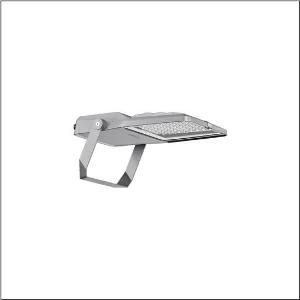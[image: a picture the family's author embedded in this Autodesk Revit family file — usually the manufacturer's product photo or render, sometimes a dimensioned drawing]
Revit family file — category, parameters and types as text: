
# Revit family: floodlight_fl_21_iq_mini___pl64_5xa7771b2e1a_713d
name_source: partatom
category: Lighting Fixtures
units: mm (PartAtom-declared; Revit-internal decimal feet)

## family parameters
Cut with Voids When Loaded = No
Host = Face
Light Source = No
Part Type = Normal
Room Calculation Point = No
Round Connector Dimension = Use Diameter
Shared = No

## types (1)
- --- (1 x LED, 6020 lm, 45.5 W, 3000K)
    Apparent Load = 46 VA
    CIE Flux Codes = 28 80 98 100 100
    Color Rendering = 70
    Color Temperature = 3000K
    Default Elevation = 1800 mm
    Description = Floodlight FL 21 iQ mini, floodlight, primary light control with lens, of PMMA, primary optical cover: protective disc, of toughened safety glass, transparent, light distribution: PL64, light emission: direct distribution, installation type: surface-mounted, LED, High Power LED, rated luminous flux: 6.020lm, luminous efficacy: 132lm/W, light colour: 730, colour temperature: 3000K, control: Auto-Match, Temp-Guard, Lumen-Switch, Night-Set, Smart-Wire, Light-Fading, Desk-Remote (wireless, voltage-free reading and setting of iQ features in the workshop via application-optimized NFC function/RFID function), optimised constant luminous flux control (CLO 2.0), with terminal, 6-pole, mains connection: 220..240V, AC, 50/60Hz, start of lifetime: 46W, end of service life: 48W, reduction: 22W, luminaire housing, of diecast aluminium, powder-coated, Siteco® metallic grey (DB 702S), corrosivity category C5 mid according to DIN EN ISO 12944, sealing non-destructively replaceable, mounting bracket, of steel, galvanised, powder-coated, Siteco® metallic grey (DB 702S), protection rating (complete): IP66, insulation class (complete): insulation class II (safety insulation), certification: CE, ENEC, VDE, protection symbol: D, impact resistance: IK08, permissible operating ambient temperature: -40..+40°C, permissible operating ambient temperature for outdoor applications: -40..+50°C, standard: DIN EN 12944, LABS conformity tested according to VDMA 24364:2018-05, packaging unit: 1 piece

Light Distribution: PL64
    Height = 70 mm
    Lamp = 1 x LED
    Lamp Light Flux = 6020 lm
    Lamp Power = 45.5 W
    Lamp count = 1
    Length = 485 mm
    Luminous efficacy = 132 lm/W
    Manufacturer = Siteco
    ModVariant = No
    Model = 5XA7771B2E1A
    Mounting Place = Wall
    Mounting Type = Surface mounted
    Number of Poles = 1
    OnlyDefault = Yes
    Power Factor = 1
    Product Name = Floodlight FL 21 iQ mini | PL64
    Product group = floodlight | wall mounted
    ProductGroupID = 2001
    Protection Class = Protection class II
    Protection Degree = IP 66
    RLX_Detail_Level = 1
    RLX_Emergency_Light_Flux = 0 lm
    RLX_Emergency_Type = 0
    RLX_Emergency_Type_DB = No
    RlxData = <blob elided: 96197 chars, md5=8cffde66>
    Socket = socket
    Standby Power = 0 W
    System Light Flux = 6020 lm
    System Power = 46 W
    Type Comments = factory setting: luminous flux: 100 % | dim-lin: 254 | 463 mA
    Type Image = l_1006845.jpg
    URL = http://relux.com
    VarID = @adj_099525
    Voltage = 0 V
    Weight = 0.00 kg
    Width = 337 mm

## geometry (parser evidence)
native form markers: Blend x4, Sweep x11
no freeform markers — native parametric forms only
